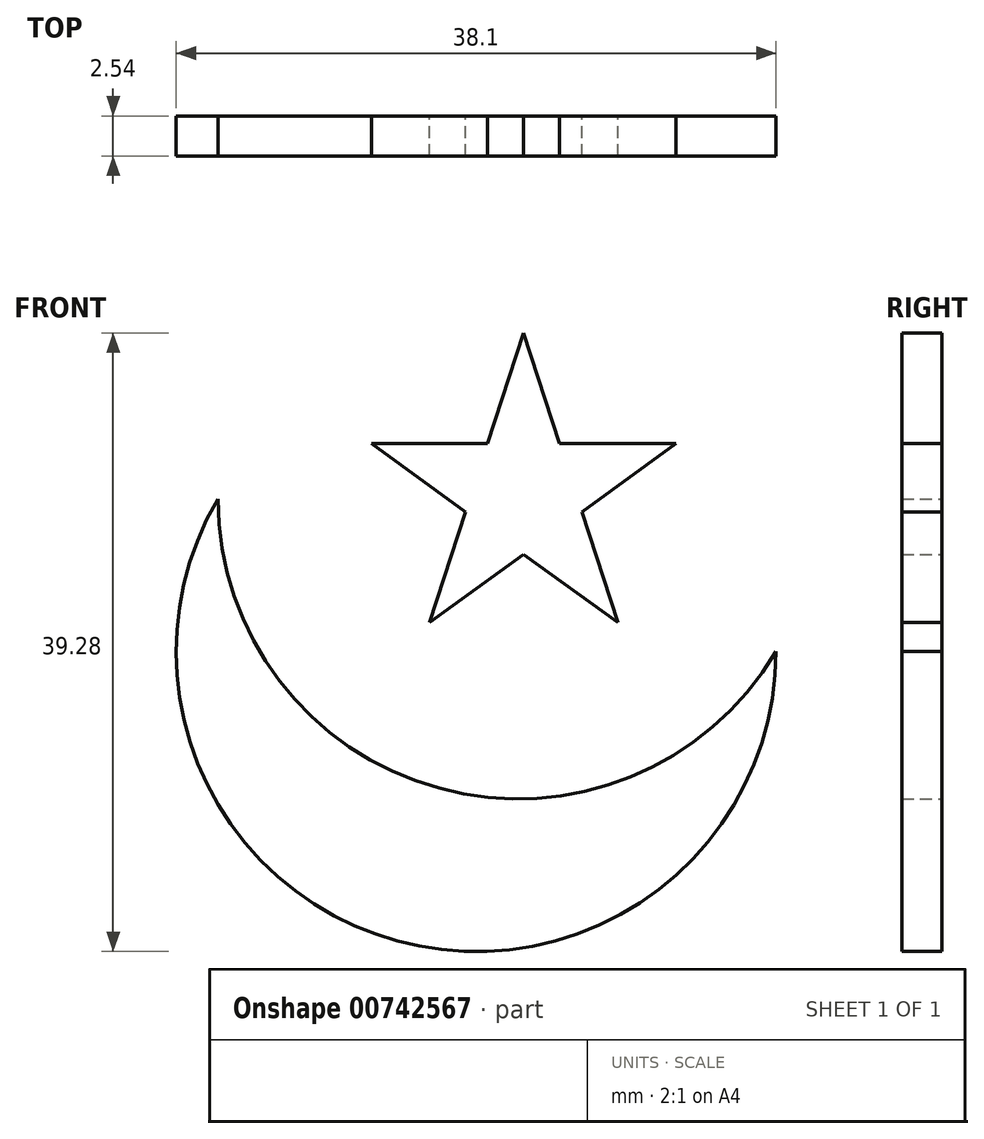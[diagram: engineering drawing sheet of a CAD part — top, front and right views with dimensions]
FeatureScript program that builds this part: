
annotation { "Feature Type Name" : "Feature", "Feature Type Description" : "" }
export const myFeature = defineFeature(function(context is Context, id is Id, definition is map)
    precondition{}
    {
        {
            var Q0;
            Q0=qCreatedBy(makeId("Front.planeOp"),FACE);
            var sketch = newSketch(context, id + "F0", { "sketchPlane" : qUnion([Q0])});
            skCircle(sketch, "E0", {"center": v(0, 0) * mm, "radius": 19.05 * mm});
            skCircle(sketch, "E1", {"center": v(2.65, 9.7) * mm, "radius": 19.05 * mm});
            skPoint(sketch, "E1.first.point", {"position": v(19.05, 0) * mm});
            skPoint(sketch, "E1.second.point", {"position": v(-13.74, 0) * mm});
            skPoint(sketch, "E1.third.point", {"position": v(-14.94, 17.01) * mm});
            skSolve(sketch);
        }
        {
            var Q0;
            {var subQ0=sQuery(id+"F0.wireOp",EDGE,"E1");var subQ1=sQuery(id+"F0.wireOp",EDGE,"E0");var subQ2=makeQuery(id+"F0.imprint","INTERSECT",VERTEX,{"disambiguationData":[OD(0.0)],"derivedFrom":[subQ1,subQ0]});Q0=makeQuery(id+"F0.imprint","IMPRINT",FACE,{"disambiguationData":[TD([[makeQuery(id+"F0.imprint","IMPRINT",EDGE,{"disambiguationData":[TD([[subQ2,-1.0]])],"derivedFrom":subQ1}),1.0]])]});}
            extrude(context, id + "F1", {"entities" : qUnion([Q0]), "depth" : 2.54 * mm, "offsetDistance" : 25.4 * mm});
        }
        {
            var Q0;
            Q0=qCreatedBy(makeId("Front.planeOp"),FACE);
            var sketch = newSketch(context, id + "F2", { "sketchPlane" : qUnion([Q0])});
            skCircle(sketch, "E2", {"center": v(3.02, 10.06) * mm, "radius": 10.17 * mm});
            skCircle(sketch, "E3.cCircle", {"center": v(3.02, 10.06) * mm, "radius": 10.17 * mm, "construction": true});
            skLineSegment(sketch, "E3.0", {"start": v(3.02, 20.23) * mm, "end": v(12.69, 13.2) * mm});
            skLineSegment(sketch, "E3.1", {"start": v(12.69, 13.2) * mm, "end": v(9, 1.84) * mm});
            skLineSegment(sketch, "E3.2", {"start": v(9, 1.84) * mm, "end": v(-2.96, 1.84) * mm});
            skLineSegment(sketch, "E3.3", {"start": v(-2.96, 1.84) * mm, "end": v(-6.65, 13.2) * mm});
            skLineSegment(sketch, "E3.4", {"start": v(-6.65, 13.2) * mm, "end": v(3.02, 20.23) * mm});
            skLineSegment(sketch, "E4", {"start": v(3.02, 20.23) * mm, "end": v(-2.96, 1.84) * mm});
            skLineSegment(sketch, "E5", {"start": v(12.69, 13.2) * mm, "end": v(-2.96, 1.84) * mm});
            skLineSegment(sketch, "E6", {"start": v(-6.65, 13.2) * mm, "end": v(12.69, 13.2) * mm});
            skLineSegment(sketch, "E7", {"start": v(-6.65, 13.2) * mm, "end": v(9, 1.84) * mm});
            skLineSegment(sketch, "E8", {"start": v(9, 1.84) * mm, "end": v(3.02, 20.23) * mm});
            skSolve(sketch);
        }
        {
            var Q0;
            {var subQ1=sQuery(id+"F2.wireOp",EDGE,"E4");var subQ3=sQuery(id+"F2.wireOp",EDGE,"E6");var subQ4=makeQuery(id+"F2.imprint","INTERSECT",VERTEX,{"derivedFrom":[subQ1,subQ3]});Q0=makeQuery(id+"F2.imprint","IMPRINT",FACE,{"disambiguationData":[TD([[makeQuery(id+"F2.imprint","IMPRINT",EDGE,{"disambiguationData":[TD([[subQ4,-1.0]])],"derivedFrom":subQ3}),1.0]])]});}
            var Q1;
            {var subQ0=sQuery(id+"F2.wireOp",EDGE,"E6");var subQ1=sQuery(id+"F2.wireOp",EDGE,"E4");var subQ2=makeQuery(id+"F2.imprint","INTERSECT",VERTEX,{"derivedFrom":[subQ1,subQ0]});Q1=makeQuery(id+"F2.imprint","IMPRINT",FACE,{"disambiguationData":[TD([[makeQuery(id+"F2.imprint","IMPRINT",EDGE,{"disambiguationData":[TD([[subQ2,-1.0]])],"derivedFrom":subQ1}),-1.0]])]});}
            var Q2;
            {var subQ1=sQuery(id+"F2.wireOp",EDGE,"E4");var subQ5=sQuery(id+"F2.wireOp",EDGE,"E6");var subQ6=makeQuery(id+"F2.imprint","INTERSECT",VERTEX,{"derivedFrom":[subQ1,subQ5]});Q2=makeQuery(id+"F2.imprint","IMPRINT",FACE,{"disambiguationData":[TD([[makeQuery(id+"F2.imprint","IMPRINT",EDGE,{"disambiguationData":[TD([[subQ6,-1.0]])],"derivedFrom":subQ1}),1.0]])]});}
            var Q3;
            {var subQ1=sQuery(id+"F2.wireOp",EDGE,"E5");var subQ3=sQuery(id+"F2.wireOp",EDGE,"E8");var subQ4=makeQuery(id+"F2.imprint","INTERSECT",VERTEX,{"derivedFrom":[subQ1,subQ3]});Q3=makeQuery(id+"F2.imprint","IMPRINT",FACE,{"disambiguationData":[TD([[makeQuery(id+"F2.imprint","IMPRINT",EDGE,{"disambiguationData":[TD([[subQ4,-1.0]])],"derivedFrom":subQ3}),-1.0]])]});}
            var Q4;
            {var subQ0=sQuery(id+"F2.wireOp",EDGE,"E8");var subQ1=sQuery(id+"F2.wireOp",EDGE,"E5");var subQ2=makeQuery(id+"F2.imprint","INTERSECT",VERTEX,{"derivedFrom":[subQ1,subQ0]});Q4=makeQuery(id+"F2.imprint","IMPRINT",FACE,{"disambiguationData":[TD([[makeQuery(id+"F2.imprint","IMPRINT",EDGE,{"disambiguationData":[TD([[subQ2,-1.0]])],"derivedFrom":subQ1}),1.0]])]});}
            var Q5;
            {var subQ1=sQuery(id+"F2.wireOp",EDGE,"E4");var subQ3=sQuery(id+"F2.wireOp",EDGE,"E7");var subQ4=makeQuery(id+"F2.imprint","INTERSECT",VERTEX,{"derivedFrom":[subQ1,subQ3]});Q5=makeQuery(id+"F2.imprint","IMPRINT",FACE,{"disambiguationData":[TD([[makeQuery(id+"F2.imprint","IMPRINT",EDGE,{"disambiguationData":[TD([[subQ4,-1.0]])],"derivedFrom":subQ3}),-1.0]])]});}
            extrude(context, id + "F3", {"entities" : qUnion([Q0, Q1, Q2, Q3, Q4, Q5]), "depth" : 2.54 * mm, "offsetDistance" : 25.4 * mm});
        }
    });
